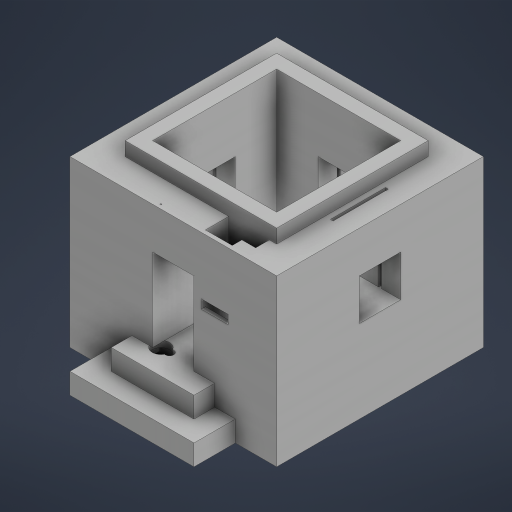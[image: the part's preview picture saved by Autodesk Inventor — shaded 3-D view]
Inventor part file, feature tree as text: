
AUTODESK INVENTOR PART (.ipt)
format: ipt  version: 2023 (Build 270158000, 158)  size: 482,816 bytes
history: native  units: mm
features: sketch x17, extrude x16, other x1, hole x1
ambient origin geometry x8: Origin, YZ Plane, XZ Plane, XY Plane, X Axis, Y Axis, Z Axis, Center Point
bodies: Body1 (feature_tree)
feature tree (35):
  other  "Těleso1"
  extrude  "Vysunutí1"  Depth=150.0mm
  extrude  "Vysunutí2"  Depth=150.0mm
  extrude  "Vysunutí3"  Depth=30.0mm TaperAngle=0.0deg
  extrude  "Vysunutí4"  Depth=150.0mm
  extrude  "Vysunutí5"  Depth=150.0mm
  extrude  "Vysunutí6"  Depth=90.0mm
  extrude  "Vysunutí7"  Depth=90.0mm
  hole  "Díra1"  [1 undecoded]
  extrude  "Vysunutí9"  Depth=30.0mm
  extrude  "Vysunutí10"  Depth=60.0mm
  extrude  "Vysunutí12"  Depth=90.0mm TaperAngle=0.0deg
  extrude  "Vysunutí14"  Depth=30.0mm
  extrude  "Vysunutí15"  Depth=30.0mm
  extrude  "Vysunutí16"  Depth=30.0mm TaperAngle=0.0deg
  extrude  "Vysunutí17"  Depth=30.0mm
  extrude  "Vysunutí18"  Depth=30.0mm
  extrude  "Vysunutí19"  TaperAngle=0.0deg  [1 undecoded]
  sketch  "Náčrt1"
  sketch  "Náčrt2"
  sketch  "Náčrt3"
  sketch  "Náčrt4"
  sketch  "Náčrt5"
  sketch  "Náčrt6"
  sketch  "Náčrt7"
  sketch  "Náčrt9"
  sketch  "Náčrt10"
  sketch  "Náčrt11"
  sketch  "Náčrt13"
  sketch  "Náčrt15"
  sketch  "Náčrt16"
  sketch  "Náčrt17"
  sketch  "Náčrt18"
  sketch  "Náčrt19"
  sketch  "Náčrt20"
note: 2 required parameter values undecoded (feature->parameter linkage not recoverable at this tier; creation-order binding heuristic only, values carry confidence <= 0.55)
